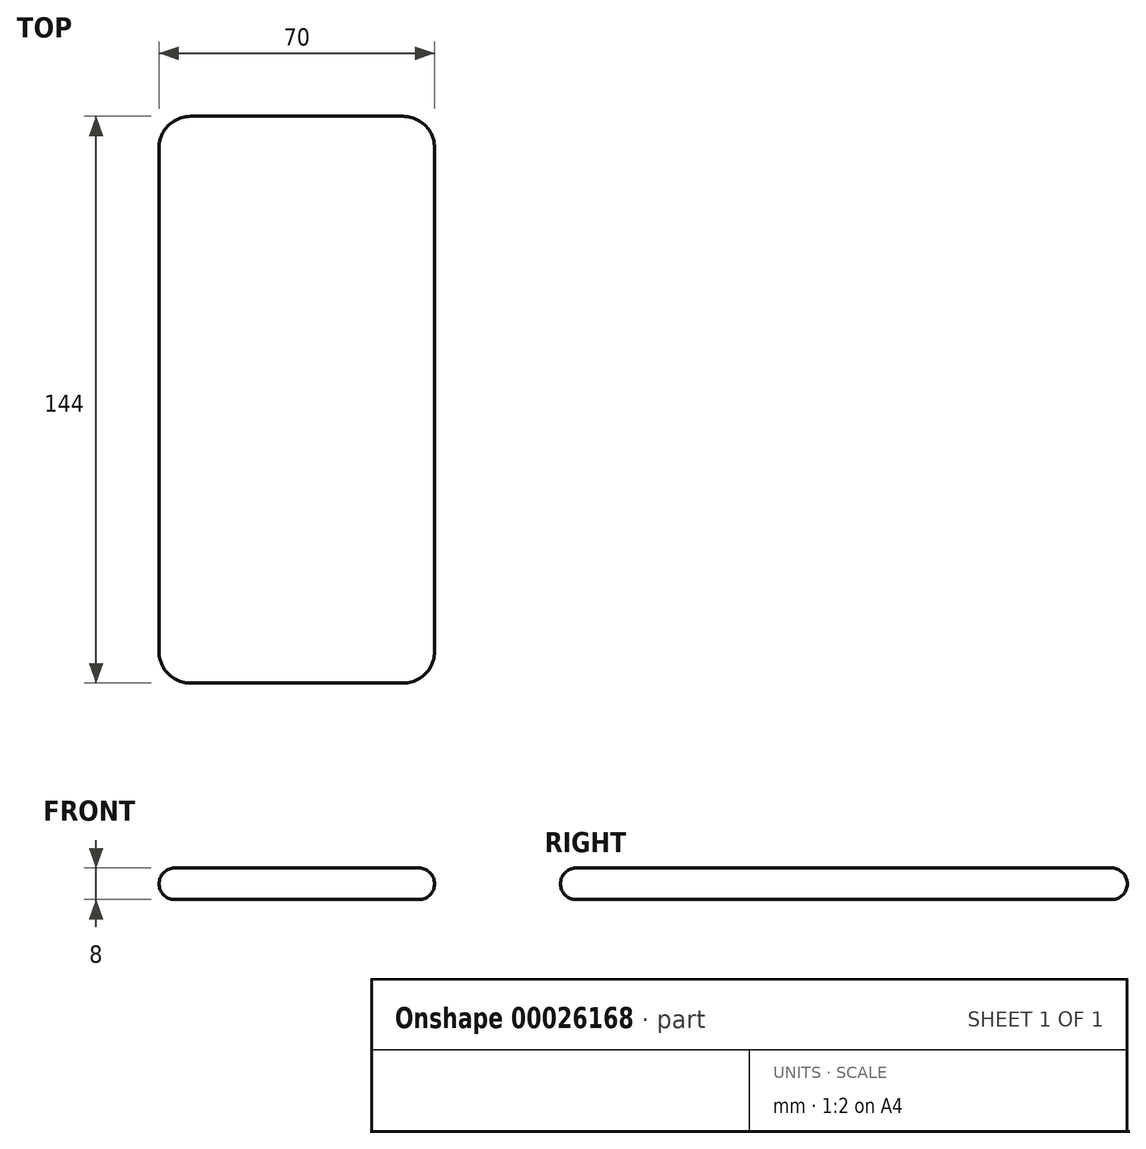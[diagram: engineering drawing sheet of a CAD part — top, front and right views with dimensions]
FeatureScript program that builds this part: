
annotation { "Feature Type Name" : "Feature", "Feature Type Description" : "" }
export const myFeature = defineFeature(function(context is Context, id is Id, definition is map)
    precondition{}
    {
        {
            var Q0;
            Q0=qCreatedBy(makeId("Top.planeOp"),FACE);
            var sketch = newSketch(context, id + "F0", { "sketchPlane" : qUnion([Q0])});
            skLineSegment(sketch, "E0.rect.bottom", {"start": v(35, -72) * mm, "end": v(-35, -72) * mm});
            skLineSegment(sketch, "E0.rect.top", {"start": v(35, 72) * mm, "end": v(-35, 72) * mm});
            skLineSegment(sketch, "E0.rect.left", {"start": v(35, -72) * mm, "end": v(35, 72) * mm});
            skLineSegment(sketch, "E0.rect.right", {"start": v(-35, -72) * mm, "end": v(-35, 72) * mm});
            skPoint(sketch, "E0.rect.middle", {"position": v(0, 0) * mm});
            skSolve(sketch);
        }
        {
            var Q0;
            Q0 = qSketchRegion(id + "F0", true);
            extrude(context, id + "F1", {"entities" : qUnion([Q0]), "depth" : 8 * mm});
        }
        {
            var Q0;
            Q0=makeQuery(id+"F1.opExtrude","SWEPT_EDGE",EDGE,{"disambiguationData":[OSD([sQuery(id+"F0.wireOp",EDGE,"E0.rect.bottom"),sQuery(id+"F0.wireOp",EDGE,"E0.rect.left")])]});
            var Q1;
            Q1=makeQuery(id+"F1.opExtrude","SWEPT_EDGE",EDGE,{"disambiguationData":[OSD([sQuery(id+"F0.wireOp",EDGE,"E0.rect.top"),sQuery(id+"F0.wireOp",EDGE,"E0.rect.left")])]});
            var Q2;
            Q2=makeQuery(id+"F1.opExtrude","SWEPT_EDGE",EDGE,{"disambiguationData":[OSD([sQuery(id+"F0.wireOp",EDGE,"E0.rect.bottom"),sQuery(id+"F0.wireOp",EDGE,"E0.rect.right")])]});
            var Q3;
            Q3=makeQuery(id+"F1.opExtrude","SWEPT_EDGE",EDGE,{"disambiguationData":[OSD([sQuery(id+"F0.wireOp",EDGE,"E0.rect.top"),sQuery(id+"F0.wireOp",EDGE,"E0.rect.right")])]});
            fillet(context, id + "F2", {"entities" : qUnion([Q0, Q1, Q2, Q3]), "radius" : 8 * mm, "tangentPropagation" : true, "allowEdgeOverflow" : false});
        }
        {
            var Q0;
            Q0=makeQuery(id+"F1.opExtrude","CAP_EDGE",EDGE,{"disambiguationData":[OSD([sQuery(id+"F0.wireOp",EDGE,"E0.rect.left")])],"isStart":false});
            var Q1;
            Q1=makeQuery(id+"F1.opExtrude","CAP_EDGE",EDGE,{"disambiguationData":[OSD([sQuery(id+"F0.wireOp",EDGE,"E0.rect.bottom")])],"isStart":false});
            var Q2;
            Q2=makeQuery(id+"F1.opExtrude","CAP_EDGE",EDGE,{"disambiguationData":[OSD([sQuery(id+"F0.wireOp",EDGE,"E0.rect.bottom")])],"isStart":true});
            var Q3;
            Q3=makeQuery(id+"F1.opExtrude","CAP_EDGE",EDGE,{"disambiguationData":[OSD([sQuery(id+"F0.wireOp",EDGE,"E0.rect.left")])],"isStart":true});
            var Q4;
            Q4=makeQuery(id+"F1.opExtrude","CAP_EDGE",EDGE,{"disambiguationData":[OSD([sQuery(id+"F0.wireOp",EDGE,"E0.rect.top")])],"isStart":false});
            var Q5;
            Q5=makeQuery(id+"F1.opExtrude","CAP_EDGE",EDGE,{"disambiguationData":[OSD([sQuery(id+"F0.wireOp",EDGE,"E0.rect.top")])],"isStart":true});
            var Q6;
            Q6=makeQuery(id+"F1.opExtrude","CAP_EDGE",EDGE,{"disambiguationData":[OSD([sQuery(id+"F0.wireOp",EDGE,"E0.rect.right")])],"isStart":false});
            var Q7;
            Q7=makeQuery(id+"F1.opExtrude","CAP_EDGE",EDGE,{"disambiguationData":[OSD([sQuery(id+"F0.wireOp",EDGE,"E0.rect.right")])],"isStart":true});
            fillet(context, id + "F3", {"entities" : qUnion([Q0, Q1, Q2, Q3, Q4, Q5, Q6, Q7]), "radius" : 4 * mm, "tangentPropagation" : true, "allowEdgeOverflow" : false});
        }
    });
